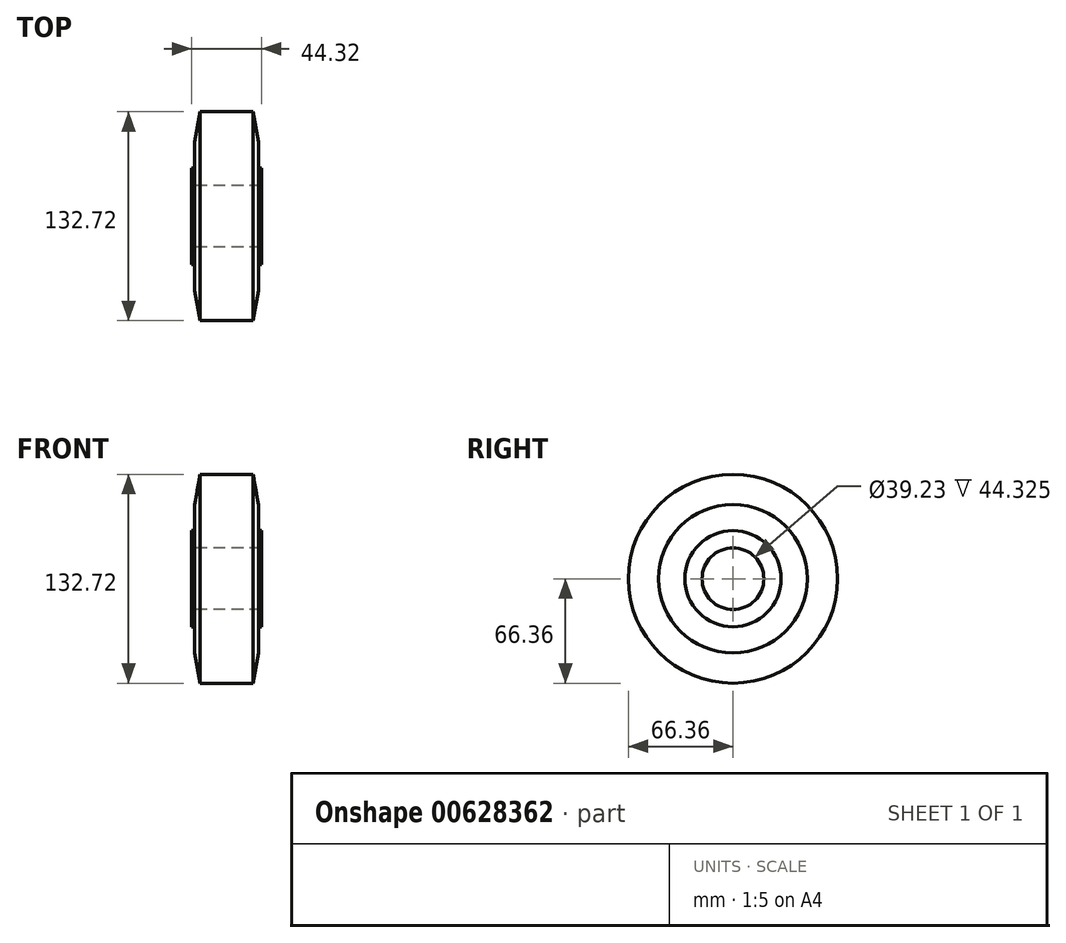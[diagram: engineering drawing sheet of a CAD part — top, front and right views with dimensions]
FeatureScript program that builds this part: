
annotation { "Feature Type Name" : "Feature", "Feature Type Description" : "" }
export const myFeature = defineFeature(function(context is Context, id is Id, definition is map)
    precondition{}
    {
        {
            var Q0;
            Q0=qCreatedBy(makeId("Front.planeOp"),FACE);
            var sketch = newSketch(context, id + "F0", { "sketchPlane" : qUnion([Q0])});
            skLineSegment(sketch, "E0", {"start": v(-76.8, 0) * mm, "end": v(74.5, 0) * mm, "construction": true});
            skLineSegment(sketch, "E1", {"start": v(0, 66.36) * mm, "end": v(16.88, 66.36) * mm});
            skLineSegment(sketch, "E2", {"start": v(16.88, 66.36) * mm, "end": v(20.18, 47.2) * mm});
            skLineSegment(sketch, "E3", {"start": v(20.18, 47.2) * mm, "end": v(20.18, 30.52) * mm});
            skLineSegment(sketch, "E4", {"start": v(20.18, 30.52) * mm, "end": v(22.16, 30.52) * mm});
            skLineSegment(sketch, "E5", {"start": v(22.16, 30.52) * mm, "end": v(22.16, 19.62) * mm});
            skLineSegment(sketch, "E6.MirrorCS", {"start": v(-20.18, 30.52) * mm, "end": v(-22.16, 30.52) * mm});
            skLineSegment(sketch, "E7.MirrorCS", {"start": v(-16.88, 66.36) * mm, "end": v(-20.18, 47.2) * mm});
            skLineSegment(sketch, "E8.MirrorCS", {"start": v(0, 66.36) * mm, "end": v(-16.88, 66.36) * mm});
            skLineSegment(sketch, "E9.MirrorCS", {"start": v(-20.18, 47.2) * mm, "end": v(-20.18, 30.52) * mm});
            skLineSegment(sketch, "E10.MirrorCS", {"start": v(-22.16, 30.52) * mm, "end": v(-22.16, 19.62) * mm});
            skLineSegment(sketch, "E11", {"start": v(-22.16, 19.62) * mm, "end": v(22.16, 19.62) * mm});
            skSolve(sketch);
        }
        {
            var Q0;
            Q0 = qSketchRegion(id + "F0", true);
            var Q1;
            Q1=sQuery(id+"F0.wireOp",EDGE,"E0");
            revolve(context, id + "F1", {"entities" : qUnion([Q0]), "axis" : qUnion([Q1]), "revolveType" : RevolveType.FULL});
        }
    });
